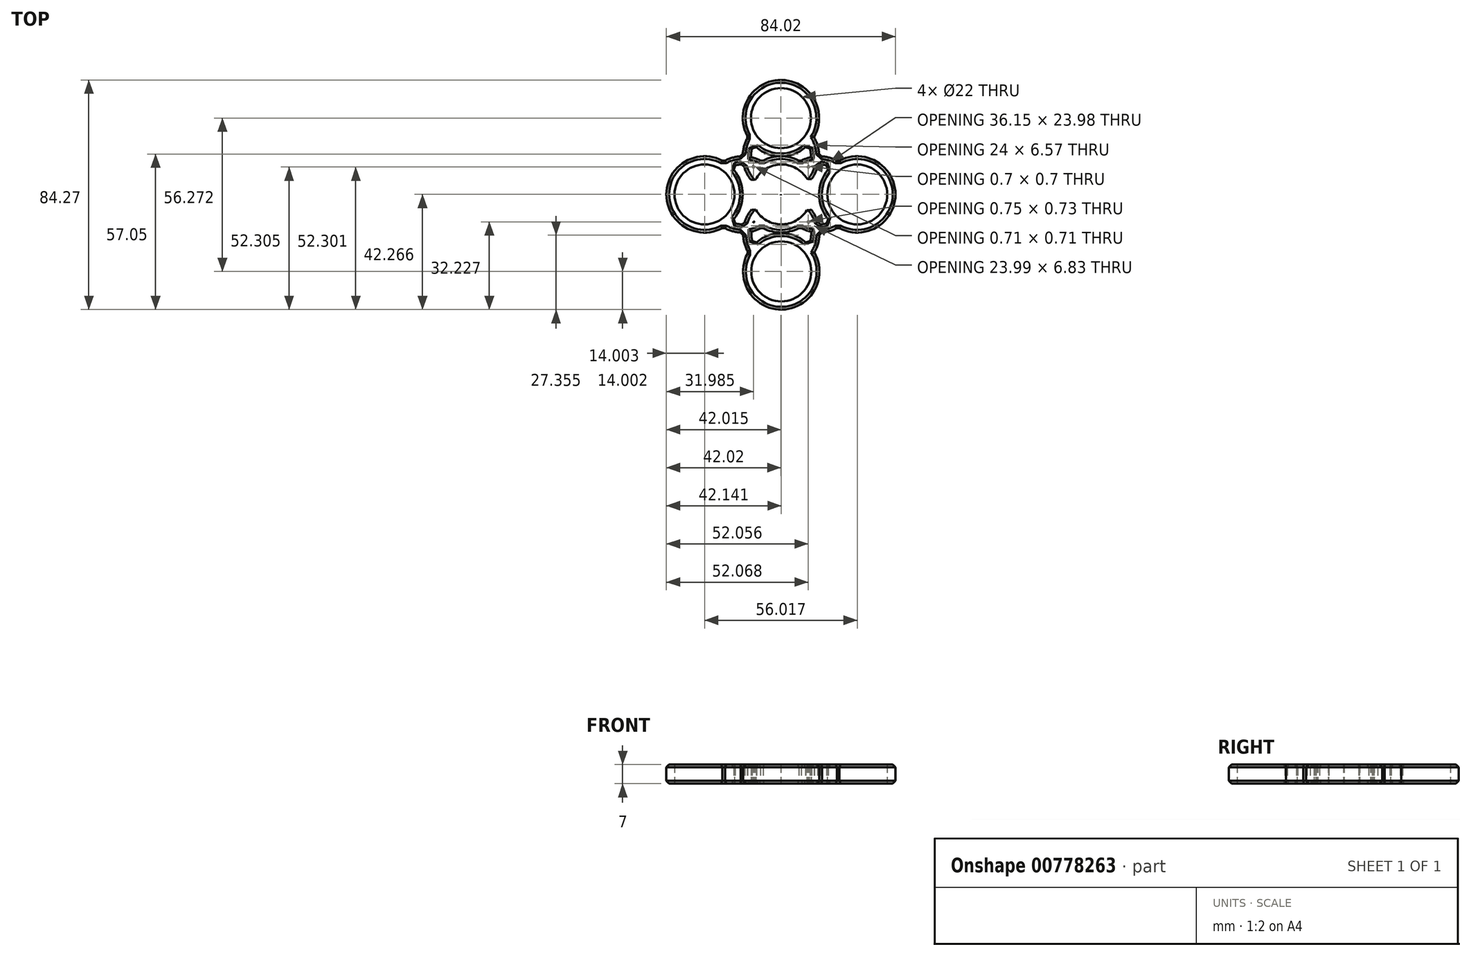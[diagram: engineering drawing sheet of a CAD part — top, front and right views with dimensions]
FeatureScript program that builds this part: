
annotation { "Feature Type Name" : "Feature", "Feature Type Description" : "" }
export const myFeature = defineFeature(function(context is Context, id is Id, definition is map)
    precondition{}
    {
        {
            var Q0;
            Q0=qCreatedBy(makeId("Top.planeOp"),FACE);
            var sketch = newSketch(context, id + "F0", { "sketchPlane" : qUnion([Q0])});
            skCircle(sketch, "E0", {"center": v(0.2, 0) * mm, "radius": 11 * mm});
            skCircle(sketch, "E1", {"center": v(0, 0) * mm, "radius": 14 * mm});
            skCircle(sketch, "E2", {"center": v(0, 28) * mm, "radius": 11 * mm});
            skCircle(sketch, "E3", {"center": v(0, 28) * mm, "radius": 14 * mm});
            skCircle(sketch, "E4", {"center": v(0, 14) * mm, "radius": 14 * mm});
            skCircle(sketch, "E5", {"center": v(0, 14) * mm, "radius": 11 * mm});
            skCircle(sketch, "E6", {"center": v(0.12, -14.26) * mm, "radius": 11 * mm});
            skCircle(sketch, "E7", {"center": v(0.12, -14.26) * mm, "radius": 14 * mm});
            skCircle(sketch, "E8", {"center": v(0.12, -28.27) * mm, "radius": 14 * mm});
            skCircle(sketch, "E9", {"center": v(0.12, -28.27) * mm, "radius": 11 * mm});
            skCircle(sketch, "E10", {"center": v(14, 0) * mm, "radius": 11 * mm});
            skCircle(sketch, "E11", {"center": v(14, 0) * mm, "radius": 14 * mm});
            skCircle(sketch, "E12", {"center": v(28, 0) * mm, "radius": 11 * mm});
            skCircle(sketch, "E13", {"center": v(28, 0) * mm, "radius": 14 * mm});
            skCircle(sketch, "E14", {"center": v(-28.02, 0) * mm, "radius": 11 * mm});
            skCircle(sketch, "E15", {"center": v(-28.02, 0) * mm, "radius": 14 * mm});
            skCircle(sketch, "E16", {"center": v(-14, 0) * mm, "radius": 11 * mm});
            skCircle(sketch, "E17", {"center": v(-14, 0) * mm, "radius": 14 * mm});
            skSolve(sketch);
        }
        {
            var Q0;
            {var subQ0=sQuery(id+"F0.wireOp",EDGE,"E17");var subQ1=sQuery(id+"F0.wireOp",EDGE,"E14");var subQ2=makeQuery(id+"F0.imprint","INTERSECT",VERTEX,{"disambiguationData":[OD(0.0)],"derivedFrom":[subQ1,subQ0]});Q0=makeQuery(id+"F0.imprint","IMPRINT",FACE,{"disambiguationData":[TD([[makeQuery(id+"F0.imprint","IMPRINT",EDGE,{"disambiguationData":[TD([[subQ2,-1.0]])],"derivedFrom":subQ1}),-1.0]])]});}
            var Q1;
            {var subQ0=sQuery(id+"F0.wireOp",EDGE,"E8");var subQ1=sQuery(id+"F0.wireOp",EDGE,"E7");var subQ2=makeQuery(id+"F0.imprint","INTERSECT",VERTEX,{"disambiguationData":[OD(0.0)],"derivedFrom":[subQ1,subQ0]});Q1=makeQuery(id+"F0.imprint","IMPRINT",FACE,{"disambiguationData":[TD([[makeQuery(id+"F0.imprint","IMPRINT",EDGE,{"disambiguationData":[TD([[subQ2,-1.0]])],"derivedFrom":subQ1}),-1.0]])]});}
            var Q2;
            {var subQ0=sQuery(id+"F0.wireOp",EDGE,"E9");var subQ1=sQuery(id+"F0.wireOp",EDGE,"E6");var subQ2=makeQuery(id+"F0.imprint","INTERSECT",VERTEX,{"disambiguationData":[OD(1.0)],"derivedFrom":[subQ1,subQ0]});Q2=makeQuery(id+"F0.imprint","IMPRINT",FACE,{"disambiguationData":[TD([[makeQuery(id+"F0.imprint","IMPRINT",EDGE,{"disambiguationData":[TD([[subQ2,-1.0]])],"derivedFrom":subQ1}),-1.0]])]});}
            var Q3;
            {var subQ0=sQuery(id+"F0.wireOp",EDGE,"E8");var subQ1=sQuery(id+"F0.wireOp",EDGE,"E6");var subQ2=makeQuery(id+"F0.imprint","INTERSECT",VERTEX,{"disambiguationData":[OD(0.0)],"derivedFrom":[subQ1,subQ0]});Q3=makeQuery(id+"F0.imprint","IMPRINT",FACE,{"disambiguationData":[TD([[makeQuery(id+"F0.imprint","IMPRINT",EDGE,{"disambiguationData":[TD([[subQ2,-1.0]])],"derivedFrom":subQ1}),1.0]])]});}
            var Q4;
            {var subQ0=sQuery(id+"F0.wireOp",EDGE,"E8");var subQ1=sQuery(id+"F0.wireOp",EDGE,"E6");var subQ2=makeQuery(id+"F0.imprint","INTERSECT",VERTEX,{"disambiguationData":[OD(0.0)],"derivedFrom":[subQ1,subQ0]});Q4=makeQuery(id+"F0.imprint","IMPRINT",FACE,{"disambiguationData":[TD([[makeQuery(id+"F0.imprint","IMPRINT",EDGE,{"disambiguationData":[TD([[subQ2,-1.0]])],"derivedFrom":subQ1}),-1.0]])]});}
            var Q5;
            {var subQ0=sQuery(id+"F0.wireOp",EDGE,"E13");var subQ2=sQuery(id+"F0.wireOp",EDGE,"E10");var subQ3=makeQuery(id+"F0.imprint","INTERSECT",VERTEX,{"disambiguationData":[OD(0.0)],"derivedFrom":[subQ2,subQ0]});Q5=makeQuery(id+"F0.imprint","IMPRINT",FACE,{"disambiguationData":[TD([[makeQuery(id+"F0.imprint","IMPRINT",EDGE,{"disambiguationData":[TD([[subQ3,1.0]])],"derivedFrom":subQ2}),1.0]])]});}
            var Q6;
            {var subQ0=sQuery(id+"F0.wireOp",EDGE,"E13");var subQ1=sQuery(id+"F0.wireOp",EDGE,"E10");var subQ2=makeQuery(id+"F0.imprint","INTERSECT",VERTEX,{"disambiguationData":[OD(1.0)],"derivedFrom":[subQ1,subQ0]});Q6=makeQuery(id+"F0.imprint","IMPRINT",FACE,{"disambiguationData":[TD([[makeQuery(id+"F0.imprint","IMPRINT",EDGE,{"disambiguationData":[TD([[subQ2,-1.0]])],"derivedFrom":subQ1}),-1.0]])]});}
            var Q7;
            {var subQ0=sQuery(id+"F0.wireOp",EDGE,"E13");var subQ1=sQuery(id+"F0.wireOp",EDGE,"E11");var subQ2=makeQuery(id+"F0.imprint","INTERSECT",VERTEX,{"disambiguationData":[OD(0.0)],"derivedFrom":[subQ1,subQ0]});Q7=makeQuery(id+"F0.imprint","IMPRINT",FACE,{"disambiguationData":[TD([[makeQuery(id+"F0.imprint","IMPRINT",EDGE,{"disambiguationData":[TD([[subQ2,1.0]])],"derivedFrom":subQ1}),-1.0]])]});}
            var Q8;
            {var subQ0=sQuery(id+"F0.wireOp",EDGE,"E13");var subQ1=sQuery(id+"F0.wireOp",EDGE,"E10");var subQ2=makeQuery(id+"F0.imprint","INTERSECT",VERTEX,{"disambiguationData":[OD(0.0)],"derivedFrom":[subQ1,subQ0]});Q8=makeQuery(id+"F0.imprint","IMPRINT",FACE,{"disambiguationData":[TD([[makeQuery(id+"F0.imprint","IMPRINT",EDGE,{"disambiguationData":[TD([[subQ2,1.0]])],"derivedFrom":subQ1}),-1.0]])]});}
            var Q9;
            {var subQ0=sQuery(id+"F0.wireOp",EDGE,"E17");var subQ1=sQuery(id+"F0.wireOp",EDGE,"E14");var subQ2=makeQuery(id+"F0.imprint","INTERSECT",VERTEX,{"disambiguationData":[OD(1.0)],"derivedFrom":[subQ1,subQ0]});Q9=makeQuery(id+"F0.imprint","IMPRINT",FACE,{"disambiguationData":[TD([[makeQuery(id+"F0.imprint","IMPRINT",EDGE,{"disambiguationData":[TD([[subQ2,-1.0]])],"derivedFrom":subQ1}),-1.0]])]});}
            var Q10;
            {var subQ0=sQuery(id+"F0.wireOp",EDGE,"E16");var subQ1=sQuery(id+"F0.wireOp",EDGE,"E14");var subQ2=makeQuery(id+"F0.imprint","INTERSECT",VERTEX,{"disambiguationData":[OD(0.0)],"derivedFrom":[subQ1,subQ0]});Q10=makeQuery(id+"F0.imprint","IMPRINT",FACE,{"disambiguationData":[TD([[makeQuery(id+"F0.imprint","IMPRINT",EDGE,{"disambiguationData":[TD([[subQ2,1.0]])],"derivedFrom":subQ1}),-1.0]])]});}
            var Q11;
            {var subQ0=sQuery(id+"F0.wireOp",EDGE,"E17");var subQ1=sQuery(id+"F0.wireOp",EDGE,"E14");var subQ2=makeQuery(id+"F0.imprint","INTERSECT",VERTEX,{"disambiguationData":[OD(0.0)],"derivedFrom":[subQ1,subQ0]});Q11=makeQuery(id+"F0.imprint","IMPRINT",FACE,{"disambiguationData":[TD([[makeQuery(id+"F0.imprint","IMPRINT",EDGE,{"disambiguationData":[TD([[subQ2,1.0]])],"derivedFrom":subQ1}),-1.0]])]});}
            var Q12;
            {var subQ0=sQuery(id+"F0.wireOp",EDGE,"E5");var subQ1=sQuery(id+"F0.wireOp",EDGE,"E2");var subQ2=makeQuery(id+"F0.imprint","INTERSECT",VERTEX,{"disambiguationData":[OD(0.0)],"derivedFrom":[subQ1,subQ0]});Q12=makeQuery(id+"F0.imprint","IMPRINT",FACE,{"disambiguationData":[TD([[makeQuery(id+"F0.imprint","IMPRINT",EDGE,{"disambiguationData":[TD([[subQ2,-1.0]])],"derivedFrom":subQ1}),-1.0]])]});}
            var Q13;
            {var subQ0=sQuery(id+"F0.wireOp",EDGE,"E5");var subQ1=sQuery(id+"F0.wireOp",EDGE,"E2");var subQ2=makeQuery(id+"F0.imprint","INTERSECT",VERTEX,{"disambiguationData":[OD(1.0)],"derivedFrom":[subQ1,subQ0]});Q13=makeQuery(id+"F0.imprint","IMPRINT",FACE,{"disambiguationData":[TD([[makeQuery(id+"F0.imprint","IMPRINT",EDGE,{"disambiguationData":[TD([[subQ2,-1.0]])],"derivedFrom":subQ1}),-1.0]])]});}
            var Q14;
            {var subQ0=sQuery(id+"F0.wireOp",EDGE,"E4");var subQ1=sQuery(id+"F0.wireOp",EDGE,"E2");var subQ2=makeQuery(id+"F0.imprint","INTERSECT",VERTEX,{"disambiguationData":[OD(0.0)],"derivedFrom":[subQ1,subQ0]});Q14=makeQuery(id+"F0.imprint","IMPRINT",FACE,{"disambiguationData":[TD([[makeQuery(id+"F0.imprint","IMPRINT",EDGE,{"disambiguationData":[TD([[subQ2,1.0]])],"derivedFrom":subQ1}),-1.0]])]});}
            var Q15;
            {var subQ0=sQuery(id+"F0.wireOp",EDGE,"E5");var subQ1=sQuery(id+"F0.wireOp",EDGE,"E2");var subQ2=makeQuery(id+"F0.imprint","INTERSECT",VERTEX,{"disambiguationData":[OD(0.0)],"derivedFrom":[subQ1,subQ0]});Q15=makeQuery(id+"F0.imprint","IMPRINT",FACE,{"disambiguationData":[TD([[makeQuery(id+"F0.imprint","IMPRINT",EDGE,{"disambiguationData":[TD([[subQ2,1.0]])],"derivedFrom":subQ1}),-1.0]])]});}
            var Q16;
            {var subQ0=sQuery(id+"F0.wireOp",EDGE,"E11");var subQ1=sQuery(id+"F0.wireOp",EDGE,"E4");var subQ2=makeQuery(id+"F0.imprint","INTERSECT",VERTEX,{"derivedFrom":[subQ1,subQ0]});Q16=makeQuery(id+"F0.imprint","IMPRINT",FACE,{"disambiguationData":[TD([[makeQuery(id+"F0.imprint","IMPRINT",EDGE,{"disambiguationData":[TD([[subQ2,1.0]])],"derivedFrom":subQ1}),-1.0]])]});}
            var Q17;
            {var subQ0=sQuery(id+"F0.wireOp",EDGE,"E4");var subQ1=sQuery(id+"F0.wireOp",EDGE,"E3");var subQ2=makeQuery(id+"F0.imprint","INTERSECT",VERTEX,{"disambiguationData":[OD(1.0)],"derivedFrom":[subQ1,subQ0]});Q17=makeQuery(id+"F0.imprint","IMPRINT",FACE,{"disambiguationData":[TD([[makeQuery(id+"F0.imprint","IMPRINT",EDGE,{"disambiguationData":[TD([[subQ2,1.0]])],"derivedFrom":subQ1}),-1.0]])]});}
            var Q18;
            {var subQ0=sQuery(id+"F0.wireOp",EDGE,"E4");var subQ1=sQuery(id+"F0.wireOp",EDGE,"E3");var subQ2=makeQuery(id+"F0.imprint","INTERSECT",VERTEX,{"disambiguationData":[OD(0.0)],"derivedFrom":[subQ1,subQ0]});Q18=makeQuery(id+"F0.imprint","IMPRINT",FACE,{"disambiguationData":[TD([[makeQuery(id+"F0.imprint","IMPRINT",EDGE,{"disambiguationData":[TD([[subQ2,-1.0]])],"derivedFrom":subQ1}),-1.0]])]});}
            var Q19;
            {var subQ0=sQuery(id+"F0.wireOp",EDGE,"E17");var subQ1=sQuery(id+"F0.wireOp",EDGE,"E4");var subQ2=makeQuery(id+"F0.imprint","INTERSECT",VERTEX,{"derivedFrom":[subQ1,subQ0]});Q19=makeQuery(id+"F0.imprint","IMPRINT",FACE,{"disambiguationData":[TD([[makeQuery(id+"F0.imprint","IMPRINT",EDGE,{"disambiguationData":[TD([[subQ2,-1.0]])],"derivedFrom":subQ1}),-1.0]])]});}
            var Q20;
            {var subQ0=sQuery(id+"F0.wireOp",EDGE,"E17");var subQ1=sQuery(id+"F0.wireOp",EDGE,"E4");var subQ2=makeQuery(id+"F0.imprint","INTERSECT",VERTEX,{"derivedFrom":[subQ1,subQ0]});Q20=makeQuery(id+"F0.imprint","IMPRINT",FACE,{"disambiguationData":[TD([[makeQuery(id+"F0.imprint","IMPRINT",EDGE,{"disambiguationData":[TD([[subQ2,-1.0]])],"derivedFrom":subQ1}),1.0]])]});}
            var Q21;
            {var subQ0=sQuery(id+"F0.wireOp",EDGE,"E17");var subQ1=sQuery(id+"F0.wireOp",EDGE,"E1");var subQ2=makeQuery(id+"F0.imprint","INTERSECT",VERTEX,{"disambiguationData":[OD(0.0)],"derivedFrom":[subQ1,subQ0]});Q21=makeQuery(id+"F0.imprint","IMPRINT",FACE,{"disambiguationData":[TD([[makeQuery(id+"F0.imprint","IMPRINT",EDGE,{"disambiguationData":[TD([[subQ2,-1.0]])],"derivedFrom":subQ1}),-1.0]])]});}
            var Q22;
            {var subQ0=sQuery(id+"F0.wireOp",EDGE,"E11");var subQ1=sQuery(id+"F0.wireOp",EDGE,"E4");var subQ2=makeQuery(id+"F0.imprint","INTERSECT",VERTEX,{"derivedFrom":[subQ1,subQ0]});Q22=makeQuery(id+"F0.imprint","IMPRINT",FACE,{"disambiguationData":[TD([[makeQuery(id+"F0.imprint","IMPRINT",EDGE,{"disambiguationData":[TD([[subQ2,1.0]])],"derivedFrom":subQ1}),1.0]])]});}
            var Q23;
            {var subQ0=sQuery(id+"F0.wireOp",EDGE,"E10");var subQ1=sQuery(id+"F0.wireOp",EDGE,"E1");var subQ2=makeQuery(id+"F0.imprint","INTERSECT",VERTEX,{"disambiguationData":[OD(0.0)],"derivedFrom":[subQ1,subQ0]});Q23=makeQuery(id+"F0.imprint","IMPRINT",FACE,{"disambiguationData":[TD([[makeQuery(id+"F0.imprint","IMPRINT",EDGE,{"disambiguationData":[TD([[subQ2,-1.0]])],"derivedFrom":subQ1}),-1.0]])]});}
            var Q24;
            {var subQ0=sQuery(id+"F0.wireOp",EDGE,"E4");var subQ1=sQuery(id+"F0.wireOp",EDGE,"E1");var subQ2=makeQuery(id+"F0.imprint","INTERSECT",VERTEX,{"disambiguationData":[OD(0.0)],"derivedFrom":[subQ1,subQ0]});Q24=makeQuery(id+"F0.imprint","IMPRINT",FACE,{"disambiguationData":[TD([[makeQuery(id+"F0.imprint","IMPRINT",EDGE,{"disambiguationData":[TD([[subQ2,-1.0]])],"derivedFrom":subQ1}),-1.0]])]});}
            var Q25;
            {var subQ0=sQuery(id+"F0.wireOp",EDGE,"E5");var subQ1=sQuery(id+"F0.wireOp",EDGE,"E0");var subQ2=makeQuery(id+"F0.imprint","INTERSECT",VERTEX,{"disambiguationData":[OD(0.0)],"derivedFrom":[subQ1,subQ0]});Q25=makeQuery(id+"F0.imprint","IMPRINT",FACE,{"disambiguationData":[TD([[makeQuery(id+"F0.imprint","IMPRINT",EDGE,{"disambiguationData":[TD([[subQ2,1.0]])],"derivedFrom":subQ1}),-1.0]])]});}
            var Q26;
            {var subQ0=sQuery(id+"F0.wireOp",EDGE,"E5");var subQ1=sQuery(id+"F0.wireOp",EDGE,"E0");var subQ2=makeQuery(id+"F0.imprint","INTERSECT",VERTEX,{"disambiguationData":[OD(0.0)],"derivedFrom":[subQ1,subQ0]});Q26=makeQuery(id+"F0.imprint","IMPRINT",FACE,{"disambiguationData":[TD([[makeQuery(id+"F0.imprint","IMPRINT",EDGE,{"disambiguationData":[TD([[subQ2,-1.0]])],"derivedFrom":subQ1}),-1.0]])]});}
            var Q27;
            {var subQ0=sQuery(id+"F0.wireOp",EDGE,"E10");var subQ1=sQuery(id+"F0.wireOp",EDGE,"E0");var subQ2=makeQuery(id+"F0.imprint","INTERSECT",VERTEX,{"disambiguationData":[OD(0.0)],"derivedFrom":[subQ1,subQ0]});Q27=makeQuery(id+"F0.imprint","IMPRINT",FACE,{"disambiguationData":[TD([[makeQuery(id+"F0.imprint","IMPRINT",EDGE,{"disambiguationData":[TD([[subQ2,-1.0]])],"derivedFrom":subQ1}),-1.0]])]});}
            var Q28;
            {var subQ0=sQuery(id+"F0.wireOp",EDGE,"E11");var subQ1=sQuery(id+"F0.wireOp",EDGE,"E0");var subQ2=makeQuery(id+"F0.imprint","INTERSECT",VERTEX,{"disambiguationData":[OD(0.0)],"derivedFrom":[subQ1,subQ0]});Q28=makeQuery(id+"F0.imprint","IMPRINT",FACE,{"disambiguationData":[TD([[makeQuery(id+"F0.imprint","IMPRINT",EDGE,{"disambiguationData":[TD([[subQ2,-1.0]])],"derivedFrom":subQ1}),-1.0]])]});}
            var Q29;
            {var subQ0=sQuery(id+"F0.wireOp",EDGE,"E17");var subQ1=sQuery(id+"F0.wireOp",EDGE,"E0");var subQ2=makeQuery(id+"F0.imprint","INTERSECT",VERTEX,{"disambiguationData":[OD(0.0)],"derivedFrom":[subQ1,subQ0]});Q29=makeQuery(id+"F0.imprint","IMPRINT",FACE,{"disambiguationData":[TD([[makeQuery(id+"F0.imprint","IMPRINT",EDGE,{"disambiguationData":[TD([[subQ2,-1.0]])],"derivedFrom":subQ1}),-1.0]])]});}
            var Q30;
            {var subQ0=sQuery(id+"F0.wireOp",EDGE,"E11");var subQ1=sQuery(id+"F0.wireOp",EDGE,"E6");var subQ2=makeQuery(id+"F0.imprint","INTERSECT",VERTEX,{"disambiguationData":[OD(0.0)],"derivedFrom":[subQ1,subQ0]});Q30=makeQuery(id+"F0.imprint","IMPRINT",FACE,{"disambiguationData":[TD([[makeQuery(id+"F0.imprint","IMPRINT",EDGE,{"disambiguationData":[TD([[subQ2,1.0]])],"derivedFrom":subQ1}),-1.0]])]});}
            var Q31;
            {var subQ0=sQuery(id+"F0.wireOp",EDGE,"E11");var subQ1=sQuery(id+"F0.wireOp",EDGE,"E7");var subQ2=makeQuery(id+"F0.imprint","INTERSECT",VERTEX,{"disambiguationData":[OD(0.0)],"derivedFrom":[subQ1,subQ0]});Q31=makeQuery(id+"F0.imprint","IMPRINT",FACE,{"disambiguationData":[TD([[makeQuery(id+"F0.imprint","IMPRINT",EDGE,{"disambiguationData":[TD([[subQ2,-1.0]])],"derivedFrom":subQ1}),-1.0]])]});}
            var Q32;
            {var subQ0=sQuery(id+"F0.wireOp",EDGE,"E17");var subQ1=sQuery(id+"F0.wireOp",EDGE,"E6");var subQ2=makeQuery(id+"F0.imprint","INTERSECT",VERTEX,{"disambiguationData":[OD(1.0)],"derivedFrom":[subQ1,subQ0]});Q32=makeQuery(id+"F0.imprint","IMPRINT",FACE,{"disambiguationData":[TD([[makeQuery(id+"F0.imprint","IMPRINT",EDGE,{"disambiguationData":[TD([[subQ2,-1.0]])],"derivedFrom":subQ1}),-1.0]])]});}
            var Q33;
            {var subQ0=sQuery(id+"F0.wireOp",EDGE,"E17");var subQ1=sQuery(id+"F0.wireOp",EDGE,"E7");var subQ2=makeQuery(id+"F0.imprint","INTERSECT",VERTEX,{"disambiguationData":[OD(0.0)],"derivedFrom":[subQ1,subQ0]});Q33=makeQuery(id+"F0.imprint","IMPRINT",FACE,{"disambiguationData":[TD([[makeQuery(id+"F0.imprint","IMPRINT",EDGE,{"disambiguationData":[TD([[subQ2,1.0]])],"derivedFrom":subQ1}),-1.0]])]});}
            var Q34;
            {var subQ0=sQuery(id+"F0.wireOp",EDGE,"E16");var subQ1=sQuery(id+"F0.wireOp",EDGE,"E6");var subQ2=makeQuery(id+"F0.imprint","INTERSECT",VERTEX,{"disambiguationData":[OD(1.0)],"derivedFrom":[subQ1,subQ0]});Q34=makeQuery(id+"F0.imprint","IMPRINT",FACE,{"disambiguationData":[TD([[makeQuery(id+"F0.imprint","IMPRINT",EDGE,{"disambiguationData":[TD([[subQ2,-1.0]])],"derivedFrom":subQ1}),-1.0]])]});}
            var Q35;
            {var subQ0=sQuery(id+"F0.wireOp",EDGE,"E7");var subQ1=sQuery(id+"F0.wireOp",EDGE,"E1");var subQ2=makeQuery(id+"F0.imprint","INTERSECT",VERTEX,{"disambiguationData":[OD(0.0)],"derivedFrom":[subQ1,subQ0]});Q35=makeQuery(id+"F0.imprint","IMPRINT",FACE,{"disambiguationData":[TD([[makeQuery(id+"F0.imprint","IMPRINT",EDGE,{"disambiguationData":[TD([[subQ2,-1.0]])],"derivedFrom":subQ1}),-1.0]])]});}
            var Q36;
            {var subQ0=sQuery(id+"F0.wireOp",EDGE,"E16");var subQ1=sQuery(id+"F0.wireOp",EDGE,"E1");var subQ2=makeQuery(id+"F0.imprint","INTERSECT",VERTEX,{"disambiguationData":[OD(1.0)],"derivedFrom":[subQ1,subQ0]});Q36=makeQuery(id+"F0.imprint","IMPRINT",FACE,{"disambiguationData":[TD([[makeQuery(id+"F0.imprint","IMPRINT",EDGE,{"disambiguationData":[TD([[subQ2,-1.0]])],"derivedFrom":subQ1}),-1.0]])]});}
            var Q37;
            {var subQ0=sQuery(id+"F0.wireOp",EDGE,"E11");var subQ1=sQuery(id+"F0.wireOp",EDGE,"E1");var subQ2=makeQuery(id+"F0.imprint","INTERSECT",VERTEX,{"disambiguationData":[OD(1.0)],"derivedFrom":[subQ1,subQ0]});Q37=makeQuery(id+"F0.imprint","IMPRINT",FACE,{"disambiguationData":[TD([[makeQuery(id+"F0.imprint","IMPRINT",EDGE,{"disambiguationData":[TD([[subQ2,-1.0]])],"derivedFrom":subQ1}),-1.0]])]});}
            var Q38;
            {var subQ0=sQuery(id+"F0.wireOp",EDGE,"E6");var subQ1=sQuery(id+"F0.wireOp",EDGE,"E1");var subQ2=makeQuery(id+"F0.imprint","INTERSECT",VERTEX,{"disambiguationData":[OD(1.0)],"derivedFrom":[subQ1,subQ0]});Q38=makeQuery(id+"F0.imprint","IMPRINT",FACE,{"disambiguationData":[TD([[makeQuery(id+"F0.imprint","IMPRINT",EDGE,{"disambiguationData":[TD([[subQ2,-1.0]])],"derivedFrom":subQ1}),-1.0]])]});}
            var Q39;
            {var subQ0=sQuery(id+"F0.wireOp",EDGE,"E10");var subQ1=sQuery(id+"F0.wireOp",EDGE,"E6");var subQ2=makeQuery(id+"F0.imprint","INTERSECT",VERTEX,{"disambiguationData":[OD(0.0)],"derivedFrom":[subQ1,subQ0]});Q39=makeQuery(id+"F0.imprint","IMPRINT",FACE,{"disambiguationData":[TD([[makeQuery(id+"F0.imprint","IMPRINT",EDGE,{"disambiguationData":[TD([[subQ2,1.0]])],"derivedFrom":subQ1}),-1.0]])]});}
            var Q40;
            {var subQ0=sQuery(id+"F0.wireOp",EDGE,"E17");var subQ1=sQuery(id+"F0.wireOp",EDGE,"E0");var subQ2=makeQuery(id+"F0.imprint","INTERSECT",VERTEX,{"disambiguationData":[OD(1.0)],"derivedFrom":[subQ1,subQ0]});Q40=makeQuery(id+"F0.imprint","IMPRINT",FACE,{"disambiguationData":[TD([[makeQuery(id+"F0.imprint","IMPRINT",EDGE,{"disambiguationData":[TD([[subQ2,-1.0]])],"derivedFrom":subQ1}),-1.0]])]});}
            var Q41;
            {var subQ0=sQuery(id+"F0.wireOp",EDGE,"E11");var subQ1=sQuery(id+"F0.wireOp",EDGE,"E0");var subQ2=makeQuery(id+"F0.imprint","INTERSECT",VERTEX,{"disambiguationData":[OD(1.0)],"derivedFrom":[subQ1,subQ0]});Q41=makeQuery(id+"F0.imprint","IMPRINT",FACE,{"disambiguationData":[TD([[makeQuery(id+"F0.imprint","IMPRINT",EDGE,{"disambiguationData":[TD([[subQ2,-1.0]])],"derivedFrom":subQ1}),-1.0]])]});}
            var Q42;
            {var subQ0=sQuery(id+"F0.wireOp",EDGE,"E6");var subQ1=sQuery(id+"F0.wireOp",EDGE,"E0");var subQ2=makeQuery(id+"F0.imprint","INTERSECT",VERTEX,{"disambiguationData":[OD(1.0)],"derivedFrom":[subQ1,subQ0]});Q42=makeQuery(id+"F0.imprint","IMPRINT",FACE,{"disambiguationData":[TD([[makeQuery(id+"F0.imprint","IMPRINT",EDGE,{"disambiguationData":[TD([[subQ2,-1.0]])],"derivedFrom":subQ1}),-1.0]])]});}
            var Q43;
            {var subQ0=sQuery(id+"F0.wireOp",EDGE,"E10");var subQ1=sQuery(id+"F0.wireOp",EDGE,"E0");var subQ2=makeQuery(id+"F0.imprint","INTERSECT",VERTEX,{"disambiguationData":[OD(1.0)],"derivedFrom":[subQ1,subQ0]});Q43=makeQuery(id+"F0.imprint","IMPRINT",FACE,{"disambiguationData":[TD([[makeQuery(id+"F0.imprint","IMPRINT",EDGE,{"disambiguationData":[TD([[subQ2,-1.0]])],"derivedFrom":subQ1}),-1.0]])]});}
            var Q44;
            {var subQ0=sQuery(id+"F0.wireOp",EDGE,"E16");var subQ1=sQuery(id+"F0.wireOp",EDGE,"E0");var subQ2=makeQuery(id+"F0.imprint","INTERSECT",VERTEX,{"disambiguationData":[OD(1.0)],"derivedFrom":[subQ1,subQ0]});Q44=makeQuery(id+"F0.imprint","IMPRINT",FACE,{"disambiguationData":[TD([[makeQuery(id+"F0.imprint","IMPRINT",EDGE,{"disambiguationData":[TD([[subQ2,-1.0]])],"derivedFrom":subQ1}),-1.0]])]});}
            var Q45;
            {var subQ0=sQuery(id+"F0.wireOp",EDGE,"E6");var subQ1=sQuery(id+"F0.wireOp",EDGE,"E0");var subQ2=makeQuery(id+"F0.imprint","INTERSECT",VERTEX,{"disambiguationData":[OD(0.0)],"derivedFrom":[subQ1,subQ0]});Q45=makeQuery(id+"F0.imprint","IMPRINT",FACE,{"disambiguationData":[TD([[makeQuery(id+"F0.imprint","IMPRINT",EDGE,{"disambiguationData":[TD([[subQ2,-1.0]])],"derivedFrom":subQ1}),-1.0]])]});}
            var Q46;
            {var subQ0=sQuery(id+"F0.wireOp",EDGE,"E7");var subQ1=sQuery(id+"F0.wireOp",EDGE,"E0");var subQ2=makeQuery(id+"F0.imprint","INTERSECT",VERTEX,{"disambiguationData":[OD(0.0)],"derivedFrom":[subQ1,subQ0]});Q46=makeQuery(id+"F0.imprint","IMPRINT",FACE,{"disambiguationData":[TD([[makeQuery(id+"F0.imprint","IMPRINT",EDGE,{"disambiguationData":[TD([[subQ2,-1.0]])],"derivedFrom":subQ1}),-1.0]])]});}
            var Q47;
            {var subQ0=sQuery(id+"F0.wireOp",EDGE,"E5");var subQ1=sQuery(id+"F0.wireOp",EDGE,"E0");var subQ2=makeQuery(id+"F0.imprint","INTERSECT",VERTEX,{"disambiguationData":[OD(1.0)],"derivedFrom":[subQ1,subQ0]});Q47=makeQuery(id+"F0.imprint","IMPRINT",FACE,{"disambiguationData":[TD([[makeQuery(id+"F0.imprint","IMPRINT",EDGE,{"disambiguationData":[TD([[subQ2,-1.0]])],"derivedFrom":subQ1}),-1.0]])]});}
            var Q48;
            {var subQ0=sQuery(id+"F0.wireOp",EDGE,"E16");var subQ1=sQuery(id+"F0.wireOp",EDGE,"E0");var subQ2=makeQuery(id+"F0.imprint","INTERSECT",VERTEX,{"disambiguationData":[OD(0.0)],"derivedFrom":[subQ1,subQ0]});Q48=makeQuery(id+"F0.imprint","IMPRINT",FACE,{"disambiguationData":[TD([[makeQuery(id+"F0.imprint","IMPRINT",EDGE,{"disambiguationData":[TD([[subQ2,-1.0]])],"derivedFrom":subQ1}),-1.0]])]});}
            var Q49;
            {var subQ0=sQuery(id+"F0.wireOp",EDGE,"E5");var subQ1=sQuery(id+"F0.wireOp",EDGE,"E1");var subQ2=makeQuery(id+"F0.imprint","INTERSECT",VERTEX,{"disambiguationData":[OD(1.0)],"derivedFrom":[subQ1,subQ0]});Q49=makeQuery(id+"F0.imprint","IMPRINT",FACE,{"disambiguationData":[TD([[makeQuery(id+"F0.imprint","IMPRINT",EDGE,{"disambiguationData":[TD([[subQ2,-1.0]])],"derivedFrom":subQ1}),-1.0]])]});}
            var Q50;
            {var subQ0=sQuery(id+"F0.wireOp",EDGE,"E11");var subQ1=sQuery(id+"F0.wireOp",EDGE,"E7");var subQ2=makeQuery(id+"F0.imprint","INTERSECT",VERTEX,{"disambiguationData":[OD(1.0)],"derivedFrom":[subQ1,subQ0]});Q50=makeQuery(id+"F0.imprint","IMPRINT",FACE,{"disambiguationData":[TD([[makeQuery(id+"F0.imprint","IMPRINT",EDGE,{"disambiguationData":[TD([[subQ2,-1.0]])],"derivedFrom":subQ1}),-1.0]])]});}
            extrude(context, id + "F1", {"entities" : qUnion([Q0, Q1, Q2, Q3, Q4, Q5, Q6, Q7, Q8, Q9, Q10, Q11, Q12, Q13, Q14, Q15, Q16, Q17, Q18, Q19, Q20, Q21, Q22, Q23, Q24, Q25, Q26, Q27, Q28, Q29, Q30, Q31, Q32, Q33, Q34, Q35, Q36, Q37, Q38, Q39, Q40, Q41, Q42, Q43, Q44, Q45, Q46, Q47, Q48, Q49, Q50]), "depth" : 7 * mm, "offsetDistance" : 25.4 * mm});
        }
        {
            var Q0;
            {var subQ0=sQuery(id+"F0.wireOp",EDGE,"E13");var subQ1=sQuery(id+"F0.wireOp",EDGE,"E11");Q0=makeQuery(id+"F1.opExtrude","CAP_EDGE",EDGE,{"disambiguationData":[OSD([subQ0]),TDD([makeQuery(id+"F0.imprint","IMPRINT",EDGE,{"disambiguationData":[TD([[makeQuery(id+"F0.imprint","INTERSECT",VERTEX,{"disambiguationData":[OD(0.0)],"derivedFrom":[subQ1,subQ0]}),1.0]])],"derivedFrom":subQ0})])],"isStart":false});}
            var Q1;
            {var subQ0=sQuery(id+"F0.wireOp",EDGE,"E11");Q1=makeQuery(id+"F1.opExtrude","CAP_EDGE",EDGE,{"disambiguationData":[OSD([subQ0]),TDD([makeQuery(id+"F0.imprint","IMPRINT",EDGE,{"disambiguationData":[TD([[makeQuery(id+"F0.imprint","INTERSECT",VERTEX,{"derivedFrom":[sQuery(id+"F0.wireOp",EDGE,"E4"),subQ0]}),1.0]])],"derivedFrom":subQ0})])],"isStart":false});}
            var Q2;
            {var subQ0=sQuery(id+"F0.wireOp",EDGE,"E4");Q2=makeQuery(id+"F1.opExtrude","CAP_EDGE",EDGE,{"disambiguationData":[OSD([subQ0]),TDD([makeQuery(id+"F0.imprint","IMPRINT",EDGE,{"disambiguationData":[TD([[makeQuery(id+"F0.imprint","INTERSECT",VERTEX,{"disambiguationData":[OD(1.0)],"derivedFrom":[sQuery(id+"F0.wireOp",EDGE,"E3"),subQ0]}),1.0]])],"derivedFrom":subQ0})])],"isStart":false});}
            var Q3;
            {var subQ0=sQuery(id+"F0.wireOp",EDGE,"E4");var subQ1=sQuery(id+"F0.wireOp",EDGE,"E3");Q3=makeQuery(id+"F1.opExtrude","CAP_EDGE",EDGE,{"disambiguationData":[OSD([subQ1]),TDD([makeQuery(id+"F0.imprint","IMPRINT",EDGE,{"disambiguationData":[TD([[makeQuery(id+"F0.imprint","INTERSECT",VERTEX,{"disambiguationData":[OD(0.0)],"derivedFrom":[subQ1,subQ0]}),1.0]])],"derivedFrom":subQ1})])],"isStart":false});}
            var Q4;
            {var subQ0=sQuery(id+"F0.wireOp",EDGE,"E5");Q4=makeQuery(id+"F1.opExtrude","CAP_EDGE",EDGE,{"disambiguationData":[OSD([subQ0]),TDD([makeQuery(id+"F0.imprint","IMPRINT",EDGE,{"disambiguationData":[TD([[makeQuery(id+"F0.imprint","INTERSECT",VERTEX,{"disambiguationData":[OD(0.0)],"derivedFrom":[sQuery(id+"F0.wireOp",EDGE,"E3"),subQ0]}),-1.0]])],"derivedFrom":subQ0})])],"isStart":false});}
            var Q5;
            {var subQ0=sQuery(id+"F0.wireOp",EDGE,"E17");Q5=makeQuery(id+"F1.opExtrude","CAP_EDGE",EDGE,{"disambiguationData":[OSD([subQ0]),TDD([makeQuery(id+"F0.imprint","IMPRINT",EDGE,{"disambiguationData":[TD([[makeQuery(id+"F0.imprint","INTERSECT",VERTEX,{"disambiguationData":[OD(0.0)],"derivedFrom":[sQuery(id+"F0.wireOp",EDGE,"E1"),subQ0]}),-1.0]])],"derivedFrom":subQ0})])],"isStart":false});}
            var Q6;
            {var subQ0=sQuery(id+"F0.wireOp",EDGE,"E1");Q6=makeQuery(id+"F1.opExtrude","CAP_EDGE",EDGE,{"disambiguationData":[OSD([subQ0]),TDD([makeQuery(id+"F0.imprint","IMPRINT",EDGE,{"disambiguationData":[TD([[makeQuery(id+"F0.imprint","INTERSECT",VERTEX,{"disambiguationData":[OD(0.0)],"derivedFrom":[subQ0,sQuery(id+"F0.wireOp",EDGE,"E11")]}),-1.0]])],"derivedFrom":subQ0})])],"isStart":false});}
            var Q7;
            {var subQ0=sQuery(id+"F0.wireOp",EDGE,"E5");var subQ1=sQuery(id+"F0.wireOp",EDGE,"E3");Q7=makeQuery(id+"F1.opExtrude","CAP_EDGE",EDGE,{"disambiguationData":[OSD([subQ1]),TDD([makeQuery(id+"F0.imprint","IMPRINT",EDGE,{"disambiguationData":[TD([[makeQuery(id+"F0.imprint","INTERSECT",VERTEX,{"disambiguationData":[OD(0.0)],"derivedFrom":[subQ1,subQ0]}),-1.0]])],"derivedFrom":subQ1})])],"isStart":false});}
            var Q8;
            {var subQ0=sQuery(id+"F0.wireOp",EDGE,"E11");Q8=makeQuery(id+"F1.opExtrude","CAP_EDGE",EDGE,{"disambiguationData":[OSD([subQ0]),TDD([makeQuery(id+"F0.imprint","IMPRINT",EDGE,{"disambiguationData":[TD([[makeQuery(id+"F0.imprint","INTERSECT",VERTEX,{"disambiguationData":[OD(0.0)],"derivedFrom":[sQuery(id+"F0.wireOp",EDGE,"E1"),subQ0]}),1.0]])],"derivedFrom":subQ0})])],"isStart":false});}
            var Q9;
            {var subQ0=sQuery(id+"F0.wireOp",EDGE,"E5");Q9=makeQuery(id+"F1.opExtrude","CAP_EDGE",EDGE,{"disambiguationData":[OSD([subQ0]),TDD([makeQuery(id+"F0.imprint","IMPRINT",EDGE,{"disambiguationData":[TD([[makeQuery(id+"F0.imprint","INTERSECT",VERTEX,{"disambiguationData":[OD(1.0)],"derivedFrom":[sQuery(id+"F0.wireOp",EDGE,"E3"),subQ0]}),1.0]])],"derivedFrom":subQ0})])],"isStart":false});}
            var Q10;
            {var subQ0=sQuery(id+"F0.wireOp",EDGE,"E4");Q10=makeQuery(id+"F1.opExtrude","CAP_EDGE",EDGE,{"disambiguationData":[OSD([subQ0]),TDD([makeQuery(id+"F0.imprint","IMPRINT",EDGE,{"disambiguationData":[TD([[makeQuery(id+"F0.imprint","INTERSECT",VERTEX,{"disambiguationData":[OD(0.0)],"derivedFrom":[sQuery(id+"F0.wireOp",EDGE,"E3"),subQ0]}),-1.0]])],"derivedFrom":subQ0})])],"isStart":false});}
            var Q11;
            {var subQ0=sQuery(id+"F0.wireOp",EDGE,"E4");Q11=makeQuery(id+"F1.opExtrude","SWEPT_FACE",FACE,{"disambiguationData":[OSD([subQ0]),TDD([makeQuery(id+"F0.imprint","IMPRINT",EDGE,{"disambiguationData":[TD([[makeQuery(id+"F0.imprint","INTERSECT",VERTEX,{"disambiguationData":[OD(0.0)],"derivedFrom":[sQuery(id+"F0.wireOp",EDGE,"E3"),subQ0]}),-1.0]])],"derivedFrom":subQ0})])]});}
            var Q12;
            {var subQ0=sQuery(id+"F0.wireOp",EDGE,"E17");var subQ1=sQuery(id+"F0.wireOp",EDGE,"E15");Q12=makeQuery(id+"F1.opExtrude","SWEPT_FACE",FACE,{"disambiguationData":[OSD([subQ1]),TDD([makeQuery(id+"F0.imprint","IMPRINT",EDGE,{"disambiguationData":[TD([[makeQuery(id+"F0.imprint","INTERSECT",VERTEX,{"disambiguationData":[OD(0.0)],"derivedFrom":[subQ1,subQ0]}),-1.0]])],"derivedFrom":subQ1})])]});}
            var Q13;
            {var subQ0=sQuery(id+"F0.wireOp",EDGE,"E7");Q13=makeQuery(id+"F1.opExtrude","SWEPT_FACE",FACE,{"disambiguationData":[OSD([subQ0]),TDD([makeQuery(id+"F0.imprint","IMPRINT",EDGE,{"disambiguationData":[TD([[makeQuery(id+"F0.imprint","INTERSECT",VERTEX,{"disambiguationData":[OD(0.0)],"derivedFrom":[subQ0,sQuery(id+"F0.wireOp",EDGE,"E17")]}),-1.0]])],"derivedFrom":subQ0})])]});}
            var Q14;
            {var subQ0=sQuery(id+"F0.wireOp",EDGE,"E11");Q14=makeQuery(id+"F1.opExtrude","SWEPT_FACE",FACE,{"disambiguationData":[OSD([subQ0]),TDD([makeQuery(id+"F0.imprint","IMPRINT",EDGE,{"disambiguationData":[TD([[makeQuery(id+"F0.imprint","INTERSECT",VERTEX,{"disambiguationData":[OD(0.0)],"derivedFrom":[sQuery(id+"F0.wireOp",EDGE,"E7"),subQ0]}),-1.0]])],"derivedFrom":subQ0})])]});}
            var Q15;
            {var subQ0=sQuery(id+"F0.wireOp",EDGE,"E8");var subQ1=sQuery(id+"F0.wireOp",EDGE,"E6");Q15=makeQuery(id+"F1.opExtrude","CAP_EDGE",EDGE,{"disambiguationData":[OSD([subQ0]),TDD([makeQuery(id+"F0.imprint","IMPRINT",EDGE,{"disambiguationData":[TD([[makeQuery(id+"F0.imprint","INTERSECT",VERTEX,{"disambiguationData":[OD(0.0)],"derivedFrom":[subQ1,subQ0]}),1.0]])],"derivedFrom":subQ0})])],"isStart":true});}
            var Q16;
            {var subQ0=sQuery(id+"F0.wireOp",EDGE,"E8");var subQ1=sQuery(id+"F0.wireOp",EDGE,"E6");Q16=makeQuery(id+"F1.opExtrude","SWEPT_FACE",FACE,{"disambiguationData":[OSD([subQ0]),TDD([makeQuery(id+"F0.imprint","IMPRINT",EDGE,{"disambiguationData":[TD([[makeQuery(id+"F0.imprint","INTERSECT",VERTEX,{"disambiguationData":[OD(0.0)],"derivedFrom":[subQ1,subQ0]}),1.0]])],"derivedFrom":subQ0})])]});}
            var Q17;
            {var subQ0=sQuery(id+"F0.wireOp",EDGE,"E1");Q17=makeQuery(id+"F1.opExtrude","SWEPT_FACE",FACE,{"disambiguationData":[OSD([subQ0]),TDD([makeQuery(id+"F0.imprint","IMPRINT",EDGE,{"disambiguationData":[TD([[makeQuery(id+"F0.imprint","INTERSECT",VERTEX,{"disambiguationData":[OD(1.0)],"derivedFrom":[subQ0,sQuery(id+"F0.wireOp",EDGE,"E17")]}),-1.0]])],"derivedFrom":subQ0})])]});}
            var Q18;
            {var subQ0=sQuery(id+"F0.wireOp",EDGE,"E1");Q18=makeQuery(id+"F1.opExtrude","SWEPT_FACE",FACE,{"disambiguationData":[OSD([subQ0]),TDD([makeQuery(id+"F0.imprint","IMPRINT",EDGE,{"disambiguationData":[TD([[makeQuery(id+"F0.imprint","INTERSECT",VERTEX,{"disambiguationData":[OD(0.0)],"derivedFrom":[subQ0,sQuery(id+"F0.wireOp",EDGE,"E11")]}),-1.0]])],"derivedFrom":subQ0})])]});}
            var Q19;
            {var subQ0=sQuery(id+"F0.wireOp",EDGE,"E5");var subQ1=sQuery(id+"F0.wireOp",EDGE,"E3");Q19=makeQuery(id+"F1.opExtrude","SWEPT_FACE",FACE,{"disambiguationData":[OSD([subQ1]),TDD([makeQuery(id+"F0.imprint","IMPRINT",EDGE,{"disambiguationData":[TD([[makeQuery(id+"F0.imprint","INTERSECT",VERTEX,{"disambiguationData":[OD(0.0)],"derivedFrom":[subQ1,subQ0]}),-1.0]])],"derivedFrom":subQ1})])]});}
            var Q20;
            {var subQ0=sQuery(id+"F0.wireOp",EDGE,"E11");Q20=makeQuery(id+"F1.opExtrude","SWEPT_FACE",FACE,{"disambiguationData":[OSD([subQ0]),TDD([makeQuery(id+"F0.imprint","IMPRINT",EDGE,{"disambiguationData":[TD([[makeQuery(id+"F0.imprint","INTERSECT",VERTEX,{"derivedFrom":[sQuery(id+"F0.wireOp",EDGE,"E4"),subQ0]}),1.0]])],"derivedFrom":subQ0})])]});}
            var Q21;
            {var subQ0=sQuery(id+"F0.wireOp",EDGE,"E4");var subQ1=makeQuery(id+"F0.imprint","INTERSECT",VERTEX,{"disambiguationData":[OD(0.0)],"derivedFrom":[sQuery(id+"F0.wireOp",EDGE,"E1"),subQ0]});Q21=makeQuery(id+"F1.opExtrude","SWEPT_FACE",FACE,{"disambiguationData":[OSD([subQ0]),TDD([makeQuery(id+"F0.imprint","IMPRINT",EDGE,{"disambiguationData":[TD([[makeQuery(id+"F0.imprint","INTERSECT",VERTEX,{"disambiguationData":[OD(0.0)],"derivedFrom":[sQuery(id+"F0.wireOp",EDGE,"E0"),subQ0]}),-1.0]])],"derivedFrom":subQ0}),makeQuery(id+"F0.imprint","IMPRINT",EDGE,{"disambiguationData":[TD([[subQ1,-1.0]])],"derivedFrom":subQ0})])]});}
            var Q22;
            {var subQ0=sQuery(id+"F0.wireOp",EDGE,"E7");var subQ1=makeQuery(id+"F0.imprint","INTERSECT",VERTEX,{"disambiguationData":[OD(1.0)],"derivedFrom":[sQuery(id+"F0.wireOp",EDGE,"E1"),subQ0]});Q22=makeQuery(id+"F1.opExtrude","SWEPT_FACE",FACE,{"disambiguationData":[OSD([subQ0]),TDD([makeQuery(id+"F0.imprint","IMPRINT",EDGE,{"disambiguationData":[TD([[subQ1,1.0]])],"derivedFrom":subQ0}),makeQuery(id+"F0.imprint","IMPRINT",EDGE,{"disambiguationData":[TD([[makeQuery(id+"F0.imprint","INTERSECT",VERTEX,{"disambiguationData":[OD(1.0)],"derivedFrom":[sQuery(id+"F0.wireOp",EDGE,"E0"),subQ0]}),1.0]])],"derivedFrom":subQ0})])]});}
            var Q23;
            {var subQ0=sQuery(id+"F0.wireOp",EDGE,"E13");var subQ1=makeQuery(id+"F0.imprint","INTERSECT",VERTEX,{"derivedFrom":[sQuery(id+"F0.wireOp",EDGE,"E1"),subQ0]});Q23=makeQuery(id+"F1.opExtrude","SWEPT_FACE",FACE,{"disambiguationData":[OSD([subQ0]),TDD([makeQuery(id+"F0.imprint","IMPRINT",EDGE,{"disambiguationData":[TD([[subQ1,1.0]])],"derivedFrom":subQ0}),makeQuery(id+"F0.imprint","IMPRINT",EDGE,{"disambiguationData":[TD([[subQ1,-1.0]])],"derivedFrom":subQ0})])]});}
            var Q24;
            {var subQ0=sQuery(id+"F0.wireOp",EDGE,"E16");var subQ1=sQuery(id+"F0.wireOp",EDGE,"E15");Q24=makeQuery(id+"F1.opExtrude","SWEPT_FACE",FACE,{"disambiguationData":[OSD([subQ1]),TDD([makeQuery(id+"F0.imprint","IMPRINT",EDGE,{"disambiguationData":[TD([[makeQuery(id+"F0.imprint","INTERSECT",VERTEX,{"disambiguationData":[OD(0.0)],"derivedFrom":[subQ1,subQ0]}),1.0]])],"derivedFrom":subQ1})])]});}
            var Q25;
            {var subQ0=sQuery(id+"F0.wireOp",EDGE,"E4");var subQ1=makeQuery(id+"F0.imprint","INTERSECT",VERTEX,{"disambiguationData":[OD(1.0)],"derivedFrom":[sQuery(id+"F0.wireOp",EDGE,"E1"),subQ0]});Q25=makeQuery(id+"F1.opExtrude","SWEPT_FACE",FACE,{"disambiguationData":[OSD([subQ0]),TDD([makeQuery(id+"F0.imprint","IMPRINT",EDGE,{"disambiguationData":[TD([[subQ1,1.0]])],"derivedFrom":subQ0}),makeQuery(id+"F0.imprint","IMPRINT",EDGE,{"disambiguationData":[TD([[makeQuery(id+"F0.imprint","INTERSECT",VERTEX,{"disambiguationData":[OD(1.0)],"derivedFrom":[sQuery(id+"F0.wireOp",EDGE,"E0"),subQ0]}),1.0]])],"derivedFrom":subQ0})])]});}
            var Q26;
            {var subQ0=sQuery(id+"F0.wireOp",EDGE,"E7");var subQ1=makeQuery(id+"F0.imprint","INTERSECT",VERTEX,{"disambiguationData":[OD(0.0)],"derivedFrom":[sQuery(id+"F0.wireOp",EDGE,"E1"),subQ0]});Q26=makeQuery(id+"F1.opExtrude","SWEPT_FACE",FACE,{"disambiguationData":[OSD([subQ0]),TDD([makeQuery(id+"F0.imprint","IMPRINT",EDGE,{"disambiguationData":[TD([[makeQuery(id+"F0.imprint","INTERSECT",VERTEX,{"disambiguationData":[OD(0.0)],"derivedFrom":[sQuery(id+"F0.wireOp",EDGE,"E0"),subQ0]}),-1.0]])],"derivedFrom":subQ0}),makeQuery(id+"F0.imprint","IMPRINT",EDGE,{"disambiguationData":[TD([[subQ1,-1.0]])],"derivedFrom":subQ0})])]});}
            chamfer(context, id + "F2", {"entities" : qUnion([Q0, Q1, Q2, Q3, Q4, Q5, Q6, Q7, Q8, Q9, Q10, Q11, Q12, Q13, Q14, Q15, Q16, Q17, Q18, Q19, Q20, Q21, Q22, Q23, Q24, Q25, Q26]), "width" : 1 * mm, "tangentPropagation" : true});
        }
    });
